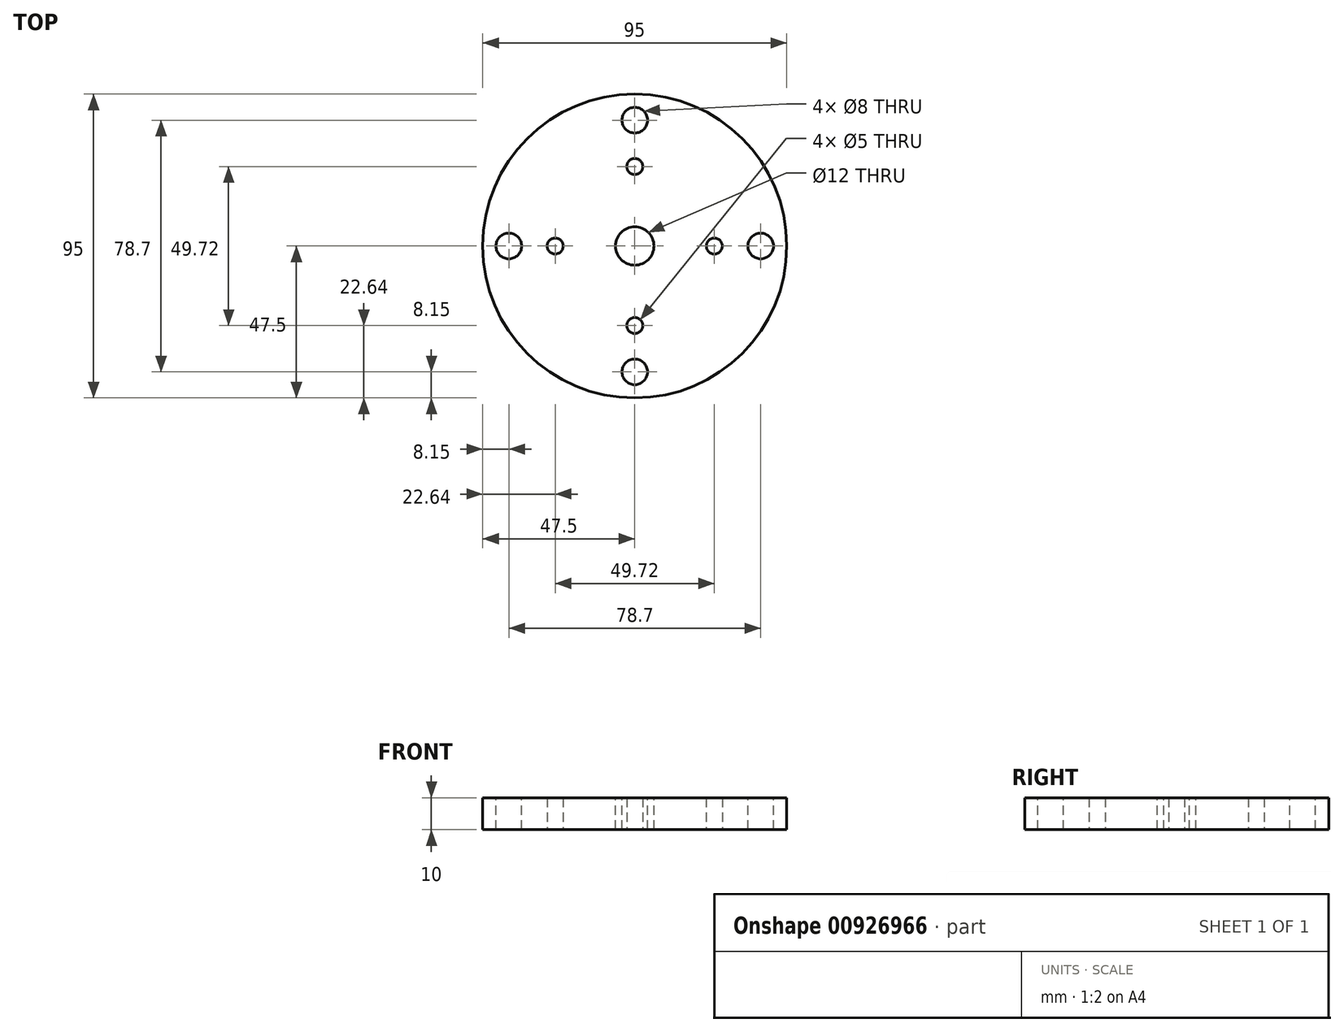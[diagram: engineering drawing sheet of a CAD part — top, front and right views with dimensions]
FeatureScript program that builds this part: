
annotation { "Feature Type Name" : "Feature", "Feature Type Description" : "" }
export const myFeature = defineFeature(function(context is Context, id is Id, definition is map)
    precondition{}
    {
        {
            var Q0;
            Q0=qCreatedBy(makeId("Top.planeOp"),FACE);
            var sketch = newSketch(context, id + "F0", { "sketchPlane" : qUnion([Q0])});
            skCircle(sketch, "E0", {"center": v(0, 0) * mm, "radius": 47.5 * mm});
            skSolve(sketch);
        }
        {
            var Q0;
            Q0=makeQuery(id+"F0.imprint","IMPRINT",FACE,{"disambiguationData":[TD([[makeQuery(id+"F0.imprint","IMPRINT",EDGE,{"derivedFrom":sQuery(id+"F0.wireOp",EDGE,"E0")}),1.0]])]});
            extrude(context, id + "F1", {"entities" : qUnion([Q0]), "depth" : 45 * mm, "offsetDistance" : 25 * mm});
        }
        {
            var Q0;
            Q0=makeQuery(id+"F1.opExtrude","CAP_FACE",FACE,{"disambiguationData":[OSD([sQuery(id+"F0.wireOp",EDGE,"E0")])],"isStart":false});
            var sketch = newSketch(context, id + "F2", { "sketchPlane" : qUnion([Q0])});
            skLineSegment(sketch, "E1.bottom", {"start": v(20.32, -20.32) * mm, "end": v(-20.32, -20.32) * mm});
            skLineSegment(sketch, "E1.top", {"start": v(20.32, 20.32) * mm, "end": v(-20.32, 20.32) * mm});
            skLineSegment(sketch, "E1.left", {"start": v(20.32, -20.32) * mm, "end": v(20.32, 20.32) * mm});
            skLineSegment(sketch, "E1.right", {"start": v(-20.32, -20.32) * mm, "end": v(-20.32, 20.32) * mm});
            skPoint(sketch, "E1.middle", {"position": v(0, 0) * mm});
            skSolve(sketch);
        }
        {
            var Q0;
            Q0=makeQuery(id+"F2.imprint","IMPRINT",FACE,{"disambiguationData":[TD([[makeQuery(id+"F2.imprint","IMPRINT",EDGE,{"derivedFrom":sQuery(id+"F2.wireOp",EDGE,"E1.bottom")}),-1.0]])]});
            extrude(context, id + "F3", {"entities" : qUnion([Q0]), "operationType" : NewBodyOperationType.REMOVE, "oppositeDirection" : true, "depth" : 35 * mm, "offsetDistance" : 25 * mm});
        }
        {
            var Q0;
            Q0=makeQuery(id+"F3.boolean.opBoolean","COPY",FACE,{"derivedFrom":makeQuery(id+"F3.opExtrude","CAP_FACE",FACE,{"disambiguationData":[OSD([sQuery(id+"F2.wireOp",EDGE,"E1.bottom"),sQuery(id+"F2.wireOp",EDGE,"E1.top"),sQuery(id+"F2.wireOp",EDGE,"E1.left"),sQuery(id+"F2.wireOp",EDGE,"E1.right")])],"isStart":false})});
            var sketch = newSketch(context, id + "F4", { "sketchPlane" : qUnion([Q0])});
            skCircle(sketch, "E2", {"center": v(0, 0) * mm, "radius": 6 * mm});
            skSolve(sketch);
        }
        {
            var Q0;
            Q0=makeQuery(id+"F1.opExtrude","CAP_FACE",FACE,{"disambiguationData":[OSD([sQuery(id+"F0.wireOp",EDGE,"E0")])],"isStart":false});
            var sketch = newSketch(context, id + "F5", { "sketchPlane" : qUnion([Q0])});
            skCircle(sketch, "E3", {"center": v(0, 0) * mm, "radius": 39.35 * mm});
            skSolve(sketch);
        }
        {
            var Q0;
            Q0=makeQuery(id+"F4.imprint","IMPRINT",FACE,{"disambiguationData":[TD([[makeQuery(id+"F4.imprint","IMPRINT",EDGE,{"derivedFrom":sQuery(id+"F4.wireOp",EDGE,"E2")}),1.0]])]});
            extrude(context, id + "F6", {"entities" : qUnion([Q0]), "operationType" : NewBodyOperationType.REMOVE, "endBound" : BoundingType.THROUGH_ALL, "oppositeDirection" : true, "depth" : 25 * mm, "offsetDistance" : 25 * mm});
        }
        {
            var Q0;
            Q0=makeQuery(id+"F1.opExtrude","CAP_FACE",FACE,{"disambiguationData":[OSD([sQuery(id+"F0.wireOp",EDGE,"E0")])],"isStart":false});
            var sketch = newSketch(context, id + "F7", { "sketchPlane" : qUnion([Q0])});
            skLineSegment(sketch, "E4.bottom", {"start": v(37.3, 29.4) * mm, "end": v(-37.3, 29.4) * mm});
            skLineSegment(sketch, "E4.top", {"start": v(37.3, 49.4) * mm, "end": v(-37.3, 49.4) * mm});
            skLineSegment(sketch, "E4.left", {"start": v(37.3, 29.4) * mm, "end": v(37.3, 49.4) * mm});
            skLineSegment(sketch, "E4.right", {"start": v(-37.3, 29.4) * mm, "end": v(-37.3, 49.4) * mm});
            skPoint(sketch, "E4.middle", {"position": v(0, 39.4) * mm});
            skLineSegment(sketch, "E5.bottom", {"start": v(37.3, -29.4) * mm, "end": v(-37.3, -29.4) * mm});
            skLineSegment(sketch, "E5.top", {"start": v(37.3, -49.4) * mm, "end": v(-37.3, -49.4) * mm});
            skLineSegment(sketch, "E5.left", {"start": v(37.3, -29.4) * mm, "end": v(37.3, -49.4) * mm});
            skLineSegment(sketch, "E5.right", {"start": v(-37.3, -29.4) * mm, "end": v(-37.3, -49.4) * mm});
            skPoint(sketch, "E5.middle", {"position": v(0, -39.4) * mm});
            skLineSegment(sketch, "E6.bottom", {"start": v(29.4, -37.3) * mm, "end": v(49.4, -37.3) * mm});
            skLineSegment(sketch, "E6.top", {"start": v(29.4, 37.3) * mm, "end": v(49.4, 37.3) * mm});
            skLineSegment(sketch, "E6.left", {"start": v(29.4, -37.3) * mm, "end": v(29.4, 37.3) * mm});
            skLineSegment(sketch, "E6.right", {"start": v(49.4, -37.3) * mm, "end": v(49.4, 37.3) * mm});
            skPoint(sketch, "E6.middle", {"position": v(39.4, 0) * mm});
            skLineSegment(sketch, "E7.bottom", {"start": v(-29.4, -37.3) * mm, "end": v(-49.4, -37.3) * mm});
            skLineSegment(sketch, "E7.top", {"start": v(-29.4, 37.3) * mm, "end": v(-49.4, 37.3) * mm});
            skLineSegment(sketch, "E7.left", {"start": v(-29.4, -37.3) * mm, "end": v(-29.4, 37.3) * mm});
            skLineSegment(sketch, "E7.right", {"start": v(-49.4, -37.3) * mm, "end": v(-49.4, 37.3) * mm});
            skPoint(sketch, "E7.middle", {"position": v(-39.4, 0) * mm});
            skSolve(sketch);
        }
        {
            var Q0;
            Q0 = qSketchRegion(id + "F7", true);
            extrude(context, id + "F8", {"entities" : qUnion([Q0]), "operationType" : NewBodyOperationType.REMOVE, "oppositeDirection" : true, "depth" : 35 * mm, "offsetDistance" : 25 * mm});
        }
        {
            var Q0;
            Q0=makeQuery(id+"F8.boolean.opBoolean","COPY",FACE,{"derivedFrom":makeQuery(id+"F8.opExtrude","CAP_FACE",FACE,{"disambiguationData":[OSD([sQuery(id+"F7.wireOp",EDGE,"E4.bottom"),sQuery(id+"F7.wireOp",EDGE,"E4.top"),sQuery(id+"F7.wireOp",EDGE,"E4.left"),sQuery(id+"F7.wireOp",EDGE,"E4.right"),sQuery(id+"F7.wireOp",EDGE,"E5.bottom"),sQuery(id+"F7.wireOp",EDGE,"E5.top"),sQuery(id+"F7.wireOp",EDGE,"E5.left"),sQuery(id+"F7.wireOp",EDGE,"E5.right"),sQuery(id+"F7.wireOp",EDGE,"E6.bottom"),sQuery(id+"F7.wireOp",EDGE,"E6.top"),sQuery(id+"F7.wireOp",EDGE,"E6.left"),sQuery(id+"F7.wireOp",EDGE,"E6.right"),sQuery(id+"F7.wireOp",EDGE,"E7.bottom"),sQuery(id+"F7.wireOp",EDGE,"E7.top"),sQuery(id+"F7.wireOp",EDGE,"E7.left"),sQuery(id+"F7.wireOp",EDGE,"E7.right")])],"isStart":false})});
            var sketch = newSketch(context, id + "F9", { "sketchPlane" : qUnion([Q0])});
            skCircle(sketch, "E8", {"center": v(0, 39.35) * mm, "radius": 4 * mm});
            skCircle(sketch, "E9", {"center": v(39.35, 0) * mm, "radius": 4 * mm});
            skCircle(sketch, "E10", {"center": v(0, -39.35) * mm, "radius": 4 * mm});
            skCircle(sketch, "E11", {"center": v(-39.35, 0) * mm, "radius": 4 * mm});
            skSolve(sketch);
        }
        {
            var Q0;
            Q0 = qSketchRegion(id + "F9", true);
            extrude(context, id + "F10", {"entities" : qUnion([Q0]), "operationType" : NewBodyOperationType.REMOVE, "endBound" : BoundingType.THROUGH_ALL, "oppositeDirection" : true, "depth" : 25 * mm, "offsetDistance" : 25 * mm});
        }
        {
            var Q0;
            Q0=makeQuery(id+"F1.opExtrude","CAP_FACE",FACE,{"disambiguationData":[OSD([sQuery(id+"F0.wireOp",EDGE,"E0")])],"isStart":false});
            extrude(context, id + "F11", {"entities" : qUnion([Q0]), "operationType" : NewBodyOperationType.REMOVE, "oppositeDirection" : true, "depth" : 35 * mm, "offsetDistance" : 25 * mm});
        }
        {
            var Q0;
            Q0=makeQuery(id+"F1.opExtrude","CAP_FACE",FACE,{"disambiguationData":[OSD([sQuery(id+"F0.wireOp",EDGE,"E0")])],"isStart":true});
            var sketch = newSketch(context, id + "F12", { "sketchPlane" : qUnion([Q0])});
            skCircle(sketch, "E12", {"center": v(0, 24.86) * mm, "radius": 2.5 * mm});
            skCircle(sketch, "E13", {"center": v(24.86, 0) * mm, "radius": 2.5 * mm});
            skCircle(sketch, "E14", {"center": v(0, -24.86) * mm, "radius": 2.5 * mm});
            skCircle(sketch, "E15", {"center": v(-24.86, 0) * mm, "radius": 2.5 * mm});
            skSolve(sketch);
        }
        {
            var Q0;
            Q0 = qSketchRegion(id + "F12", true);
            extrude(context, id + "F13", {"entities" : qUnion([Q0]), "operationType" : NewBodyOperationType.REMOVE, "endBound" : BoundingType.THROUGH_ALL, "oppositeDirection" : true, "depth" : 25 * mm, "offsetDistance" : 25 * mm});
        }
    });
